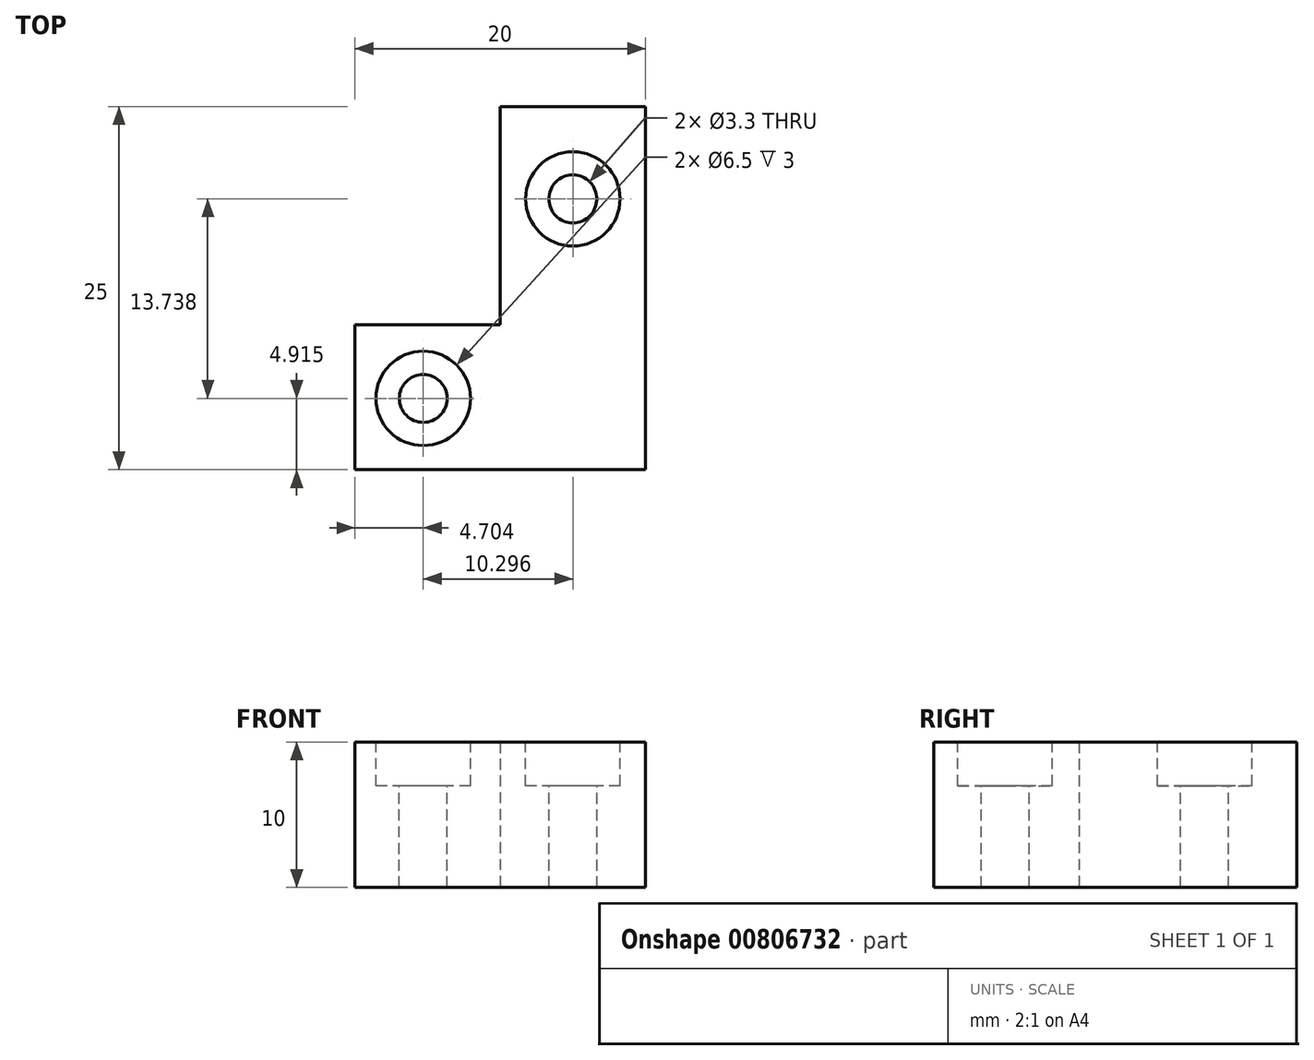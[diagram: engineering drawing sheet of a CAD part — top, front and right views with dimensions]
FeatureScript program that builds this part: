
annotation { "Feature Type Name" : "Feature", "Feature Type Description" : "" }
export const myFeature = defineFeature(function(context is Context, id is Id, definition is map)
    precondition{}
    {
        {
            var Q0;
            Q0=qCreatedBy(makeId("Front.planeOp"),FACE);
            var sketch = newSketch(context, id + "F0", { "sketchPlane" : qUnion([Q0])});
            skLineSegment(sketch, "E0.bottom", {"start": v(5, -5) * mm, "end": v(-5, -5) * mm});
            skLineSegment(sketch, "E0.top", {"start": v(5, 5) * mm, "end": v(-5, 5) * mm});
            skLineSegment(sketch, "E0.left", {"start": v(5, -5) * mm, "end": v(5, 5) * mm});
            skLineSegment(sketch, "E0.right", {"start": v(-5, -5) * mm, "end": v(-5, 5) * mm});
            skPoint(sketch, "E0.middle", {"position": v(0, 0) * mm});
            skSolve(sketch);
        }
        {
            var Q0;
            Q0=makeQuery(id+"F0.imprint","IMPRINT",FACE,{"disambiguationData":[TD([[makeQuery(id+"F0.imprint","IMPRINT",EDGE,{"derivedFrom":sQuery(id+"F0.wireOp",EDGE,"E0.bottom")}),-1.0]])]});
            extrude(context, id + "F1", {"entities" : qUnion([Q0]), "depth" : 25 * mm, "offsetDistance" : 25 * mm});
        }
        {
            var Q0;
            Q0=makeQuery(id+"F1.opExtrude","SWEPT_FACE",FACE,{"disambiguationData":[OSD([sQuery(id+"F0.wireOp",EDGE,"E0.right")])]});
            var sketch = newSketch(context, id + "F2", { "sketchPlane" : qUnion([Q0])});
            skLineSegment(sketch, "E1.bottom", {"start": v(25, 5) * mm, "end": v(15, 5) * mm});
            skLineSegment(sketch, "E1.top", {"start": v(25, -5) * mm, "end": v(15, -5) * mm});
            skLineSegment(sketch, "E1.left", {"start": v(25, 5) * mm, "end": v(25, -5) * mm});
            skLineSegment(sketch, "E1.right", {"start": v(15, 5) * mm, "end": v(15, -5) * mm});
            skSolve(sketch);
        }
        {
            var Q0;
            Q0=qSketchRegion(id+"F2",true);
            extrude(context, id + "F3", {"entities" : qUnion([Q0]), "operationType" : NewBodyOperationType.ADD, "depth" : 10 * mm, "offsetDistance" : 25 * mm});
        }
        {
            var Q0;
            Q0=makeQuery(id+"F3.boolean.opBoolean","MERGE",FACE,{"derivedFrom":[makeQuery(id+"F1.opExtrude","SWEPT_FACE",FACE,{"disambiguationData":[OSD([sQuery(id+"F0.wireOp",EDGE,"E0.top")])]}),makeQuery(id+"F3.opExtrude","SWEPT_FACE",FACE,{"disambiguationData":[OSD([sQuery(id+"F2.wireOp",EDGE,"E1.bottom")])]})]});
            var sketch = newSketch(context, id + "F4", { "sketchPlane" : qUnion([Q0])});
            skPoint(sketch, "E2", {"position": v(0, -6.35) * mm});
            skPoint(sketch, "E3", {"position": v(-10.3, -20.09) * mm});
            skSolve(sketch);
        }
        {
            var Q0;
            Q0=sQuery(id+"F4.wireOp",VERTEX,"E2");
            var Q1;
            Q1=sQuery(id+"F4.wireOp",VERTEX,"E3");
            var Q2;
            Q2=makeQuery(id+"F1.opExtrude","SWEPT_BODY",BODY,{"disambiguationData":[OSD([sQuery(id+"F0.wireOp",EDGE,"E0.bottom"),sQuery(id+"F0.wireOp",EDGE,"E0.top"),sQuery(id+"F0.wireOp",EDGE,"E0.left"),sQuery(id+"F0.wireOp",EDGE,"E0.right")])]});
            hole(context, id + "F5", {"style" : HoleStyle.C_BORE, "endStyle" : HoleEndStyle.THROUGH, "standardTappedOrClearance" : lookupTablePath({ "standard" : "ISO", "fit" : "Normal", "size" : "M3", "type" : "Clearance" }), "standardBlindInLast" : lookupTablePath({ "fit" : "Standard", "standard" : "ISO", "size" : "M3", "type" : "Clearance" }), "holeDiameter" : 3.3 * mm, "cBoreDiameter" : 6.5 * mm, "cBoreDepth" : 3 * mm, "majorDiameter" : 5 * mm, "isTappedThrough" : true, "tappedDepth" : 8 * mm, "tapClearance" : 3, "startFromSketch" : true, "locations" : qUnion([Q0, Q1]), "scope" : qUnion([Q2])});
        }
    });
